# Revit family: STH8513_27_30_40_65
name_source: partatom
category: Luminárias
units: mm (PartAtom-declared; Revit-internal decimal feet)

## family parameters
Com base no plano de trabalho = Não
Compartilhado = Não
Corte com vazios quando carregada = Não
Cota do conector redondo = Utilizar diâmetro
Fonte luminosa = Sim
Manter orientação da anotação = Não
Ponto de cálculo do ambiente = Não
Sempre na vertical = Sim
Tipo de parte = Normal

## types (4) — shared parameters
Altura = 0.05 m
Cromado = Cromado
Dimerização = Não dimerizável
Diâmetro = 0.04 m
Fabricante = Stella
Filtro de cor = 16777215
Grau de proteção (IP) = IP20
IRC (Índice de reprodução de cores) = >80
Modelo = Mini Dicroica MR11 ECO
AR70 PRO 7º 4,7W
AR 70 PRO 7º 4,7W
Potência = 3 W
Tensão Elétrica = 100V-240V
Troca de temperatura da cor de lâmpada com esmaecimento = <Nenhum>
URL = https://stella.com.br
Vidro = Vidro
Ângulo de Abertura = 36°
Ângulo de inclinação = 90.00°
zero-valued in all types: Elevação padrão

## per-type parameters (varying)
| type | Arquivo de rede fotométrica | Fluxo Luminoso | Referência | Temperatura da cor (K) |
| STH8513/27 - BIVOLT - 2700K - 240lm - 36º | STELLA - STH8513-27 - MINI DICROICA MR11 ECO 3W.ies | 240 lm | STH8513/27 - BIVOLT | 2700 K |
| STH8513/30 - BIVOLT - 3000K - 250lm - 36º | STELLA - STH8513-30 - MINI DICROICA MR11 ECO 3W.ies | 250 lm | STH8513/30 - BIVOLT | 3000 K |
| STH8513/40 - BIVOLT - 4000K - 260lm - 36° | STELLA - STH8513-40 - MINI DICROICA MR11 ECO 3W.ies | 260 lm | STH8513/40 - BIVOLT | 4000 K |
| STH8513/65 - BIVOLT - 6500K - 260lm - 36º | STELLA - STH8513-65 - MINI DICROICA MR11 ECO 3W.ies | 260 lm | STH8513/65 - BIVOLT | 6500 K |
